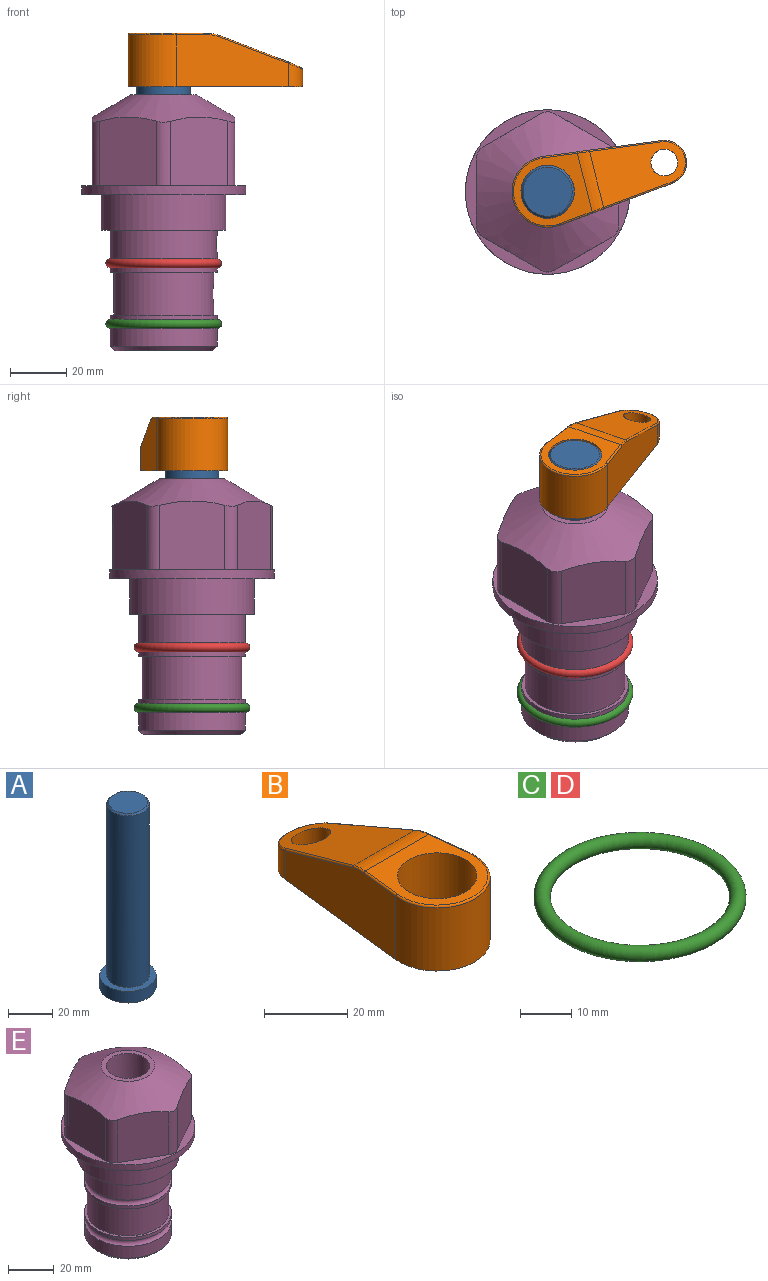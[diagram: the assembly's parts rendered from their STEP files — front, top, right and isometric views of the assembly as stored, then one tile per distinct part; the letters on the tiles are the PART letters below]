
ASSEMBLY  parts=5 mates=3
PART A: 6 faces, bbox 25.4x25.4x101.6 mm
  f0: plane 17.46x17.46mm, normal (0,0,1), area 239.5mm2, adj f5
  f1: plane 25.4x25.4mm, normal (0,0,-1), area 506.7mm2, adj f2
  f2: cylinder r=12.7mm len=25.4mm, axis (0,0,1), area 506.7mm2, adj f1,f3
  f3: plane 25.4x25.4mm, normal (0,0,1), area 221.7mm2, adj f2,f4
  f4: cylinder r=9.53mm len=94.46mm, axis (0,0,1), area 5653mm2, adj f3,f5
  f5: cone r=8.73mm half-angle=45deg, axis (0,0,-1), area 64.4mm2, adj f0,f4
PART B: 44 faces, bbox 27.5x64.5x19.1 mm
  f0: plane 2.3x0.95mm, normal (0,0,-1), area 1mm2, adj f25,f30,f34
  f1: plane 63.5x25.4mm, normal (0,0,-1), area 561.7mm2, adj f2,f3,f4,f5,f6,f7,f19,f20
  f2: cylinder r=12.7mm len=25.4mm, axis (0,0,-1), area 792.2mm2, adj f1,f3,f5,f13
  f3: plane 42.33x18.54mm, normal (0.99,0.11,0), area 647mm2, adj f1,f2,f4,f11,f12,f14
  f4: cylinder r=7.94mm len=15.78mm, axis (0,0,-1), area 158.6mm2, adj f1,f3,f5,f16
  f5: plane 42.33x18.54mm, normal (-0.99,0.11,0), area 647mm2, adj f1,f2,f4,f15,f17,f18
  f6: cylinder r=9.53mm len=19.05mm, axis (0,0,-1), area 1140.1mm2, adj f1,f8
  f7: cylinder r=4.76mm len=10.98mm, axis (0,0,-1), area 276.1mm2, adj f1,f9
  f8: plane 25.83x24.38mm, normal (0,0,1), area 262.2mm2, adj f6,f10,f11,f13,f15
  f9: plane 32.49x20.55mm, normal (0,0.34,0.94), area 489.9mm2, adj f7,f10,f14,f16,f18
  f10: cylinder r=12.7mm len=21.49mm, axis (-1,0,0), area 93.2mm2, adj f8,f9,f12,f17
  f11: cylinder r=0.51mm len=12.34mm, axis (0.11,-0.99,0), area 9.9mm2, adj f3,f8,f12,f13
  f12: bspline ~7.62x1.64mm, area 3.5mm2, adj f3,f10,f11,f14
  f13: torus R=12.19mm, axis (0,0,1), area 33.6mm2, adj f2,f8,f11,f15
  f14: cylinder r=0.51mm len=26.01mm, axis (0.1,-0.93,0.34), area 21.6mm2, adj f3,f9,f12,f16
  f15: cylinder r=0.51mm len=12.34mm, axis (0.11,0.99,0), area 9.9mm2, adj f5,f8,f13,f17
  f16: bspline ~15.78x7.05mm, area 15.7mm2, adj f4,f9,f14,f18
  f17: bspline ~7.62x1.64mm, area 3.5mm2, adj f5,f10,f15,f18
  f18: cylinder r=0.51mm len=26.01mm, axis (0.1,0.93,-0.34), area 21.6mm2, adj f5,f9,f16,f17
  f19: plane 21.6x14.29mm, normal (-0.99,-0.11,0), area 242.6mm2, adj f1,f26,f28,f34,f36,f38
  f20: plane 21.6x14.29mm, normal (0.99,-0.11,0), area 242.6mm2, adj f1,f27,f29,f37,f39,f41
  f21: cylinder r=12.7mm len=14.29mm, axis (0,0,-1), area 173.2mm2, adj f1,f26,f27,f30,f31,f33
  f22: cylinder r=7.94mm len=7.63mm, axis (0,0,-1), area 53.8mm2, adj f1,f28,f29,f42
  f23: plane 2.3x0.95mm, normal (0,0,-1), area 1mm2, adj f25,f33,f37
  f24: plane 17.94x12.32mm, normal (0,-0.34,-0.94), area 191.2mm2, adj f25,f38,f41,f42
  f25: cylinder r=9.53mm len=12.93mm, axis (-1,0,0), area 37.5mm2, adj f0,f23,f24,f31,f36,f39
  f26: cylinder r=1.59mm len=14.29mm, axis (0,0,-1), area 49mm2, adj f1,f19,f21,f32
  f27: cylinder r=1.59mm len=14.29mm, axis (0,0,-1), area 49mm2, adj f1,f20,f21,f35
  f28: cylinder r=1.59mm len=7.28mm, axis (0,0,-1), area 22.1mm2, adj f1,f19,f22,f40
  f29: cylinder r=1.59mm len=7.28mm, axis (0,0,-1), area 22.1mm2, adj f1,f20,f22,f43
  f30: torus R=14.29mm, axis (0,0,1), area 5.8mm2, adj f0,f21,f31,f32
  f31: bspline ~11.06x2.73mm, area 20.8mm2, adj f21,f25,f30,f33
  f32: sphere r=1.59mm, area 5.4mm2, adj f26,f30,f34
  f33: torus R=14.29mm, axis (0,0,1), area 5.8mm2, adj f21,f23,f31,f35
  f34: cylinder r=1.59mm len=1.68mm, axis (-0.11,0.99,0), area 2.4mm2, adj f0,f19,f32,f36
  f35: sphere r=1.59mm, area 5.4mm2, adj f27,f33,f37
  f36: bspline ~5.82x2.33mm, area 7.7mm2, adj f19,f25,f34,f38
  f37: cylinder r=1.59mm len=1.68mm, axis (0.11,0.99,0), area 2.4mm2, adj f20,f23,f35,f39
  f38: cylinder r=1.59mm len=18.33mm, axis (0.1,-0.93,0.34), area 46.7mm2, adj f19,f24,f36,f40
  f39: bspline ~5.82x2.33mm, area 7.7mm2, adj f20,f25,f37,f41
  f40: sphere r=1.59mm, area 3.6mm2, adj f28,f38,f42
  f41: cylinder r=1.59mm len=18.33mm, axis (0.1,0.93,-0.34), area 46.7mm2, adj f20,f24,f39,f43
  f42: bspline ~8.31x1.84mm, area 15.3mm2, adj f22,f24,f40,f43
  f43: sphere r=1.59mm, area 3.6mm2, adj f29,f41,f42
PART C: 1 faces, bbox 44.7x44.7x3.2 mm
  f0: torus R=19.05mm, axis (0,0,1), area 1193.9mm2
PART D: same geometry as C
PART E: 36 faces, bbox 58.7x58.7x91.2 mm
  f0: cylinder r=17.78mm len=35.56mm, axis (0,0,1), area 1670.8mm2, adj f23,f24,f31
  f1: cylinder r=19.05mm len=38.1mm, axis (0,0,1), area 1191.9mm2, adj f26,f27,f30
  f2: plane 58.66x58.66mm, normal (0,0,-1), area 1150.6mm2, adj f3,f28
  f3: cylinder r=29.33mm len=58.66mm, axis (0,0,-1), area 585.1mm2, adj f2,f4
  f4: plane 58.66x58.66mm, normal (0,0,1), area 475.9mm2, adj f3,f5,f6,f7,f8,f9,f10,f11
  f5: plane 24.5x20.32mm, normal (-0.5,0.87,0), area 562.8mm2, adj f4,f15,f16,f17
  f6: plane 24.5x20.32mm, normal (0.5,0.87,0), area 562.8mm2, adj f4,f14,f15,f17
  f7: plane 24.5x23.48mm, normal (1,0,0), area 562.8mm2, adj f4,f13,f14,f17
  f8: plane 24.5x20.32mm, normal (0.5,-0.87,0), area 562.8mm2, adj f4,f12,f13,f17
  f9: plane 24.5x20.32mm, normal (-0.5,-0.87,0), area 562.8mm2, adj f4,f11,f12,f17
  f10: plane 24.5x23.48mm, normal (-1,0,0), area 562.8mm2, adj f4,f11,f16,f17
  f11: cylinder r=5.08mm len=23.01mm, axis (0,0,-1), area 121.2mm2, adj f4,f9,f10,f17
  f12: cylinder r=5.08mm len=23.01mm, axis (0,0,-1), area 121.2mm2, adj f4,f8,f9,f17
  f13: cylinder r=5.08mm len=23.01mm, axis (0,0,-1), area 121.2mm2, adj f4,f7,f8,f17
  f14: cylinder r=5.08mm len=23.01mm, axis (0,0,-1), area 121.2mm2, adj f4,f6,f7,f17
  f15: cylinder r=5.08mm len=23.01mm, axis (0,0,-1), area 121.2mm2, adj f4,f5,f6,f17
  f16: cylinder r=5.08mm len=23.01mm, axis (0,0,-1), area 121.2mm2, adj f4,f5,f10,f17
  f17: cone r=11.73mm half-angle=60deg, axis (0,0,-1), area 2071.8mm2, adj f5,f6,f7,f8,f9,f10,f11,f12
  f18: plane 23.46x23.46mm, normal (0,0,1), area 147.4mm2, adj f17,f35
  f19: plane 34.93x34.93mm, normal (0,0,-1), area 958mm2, adj f29
  f20: cylinder r=19.05mm len=38.1mm, axis (0,0,1), area 760.1mm2, adj f21,f29
  f21: torus R=19.05mm, axis (0,0,1), area 565.3mm2, adj f20,f22
  f22: cylinder r=19.05mm len=38.1mm, axis (0,0,1), area 190mm2, adj f21,f23
  f23: plane 38.1x38.1mm, normal (0,0,1), area 146.9mm2, adj f0,f22
  f24: plane 38.1x38.1mm, normal (0,0,-1), area 146.9mm2, adj f0,f25
  f25: cylinder r=19.05mm len=38.1mm, axis (0,0,1), area 190mm2, adj f24,f26
  f26: torus R=19.05mm, axis (0,0,1), area 565.3mm2, adj f1,f25
  f27: plane 44.45x44.45mm, normal (0,0,-1), area 411.7mm2, adj f1,f28
  f28: cylinder r=22.23mm len=44.45mm, axis (0,0,1), area 1773.5mm2, adj f2,f27
  f29: cone r=19.05mm half-angle=45deg, axis (0,0,1), area 257.5mm2, adj f19,f20
  f30: cylinder r=3.17mm len=6.75mm, axis (-1,0,0), area 128mm2, adj f1,f33
  f31: cylinder r=3.17mm len=6.35mm, axis (-1,0,0), area 102.5mm2, adj f0,f33
  f32: plane 25.4x25.4mm, normal (0,0,1), area 506.7mm2, adj f33
  f33: cylinder r=12.7mm len=66.42mm, axis (0,0,-1), area 5236.2mm2, adj f30,f31,f32,f34
  f34: cone r=9.53mm half-angle=30deg, axis (0,0,-1), area 443.4mm2, adj f33,f35
  f35: cylinder r=9.53mm len=19.05mm, axis (0,0,-1), area 849mm2, adj f18,f34
PLACE A rot(axis=(0,0,1),14.1deg) t=(0,0,-16.14)mm
PLACE B rot(axis=(0,0,-1),75.9deg) t=(0,0,38.47)mm
PLACE C t=(0,0,-21.59)mm
PLACE D at identity
PLACE E at identity fixed
MATE fastened C.f0 <-> E.f0  axis (0,0,1) through (0,0,-46.1)mm
MATE cylindrical A.f2 <-> E.f0  axis (0,0,1) through (0,0,9.5)mm
MATE fastened B.f2 <-> A.f2  axis (0,0,1) through (0,0,57.52)mm
